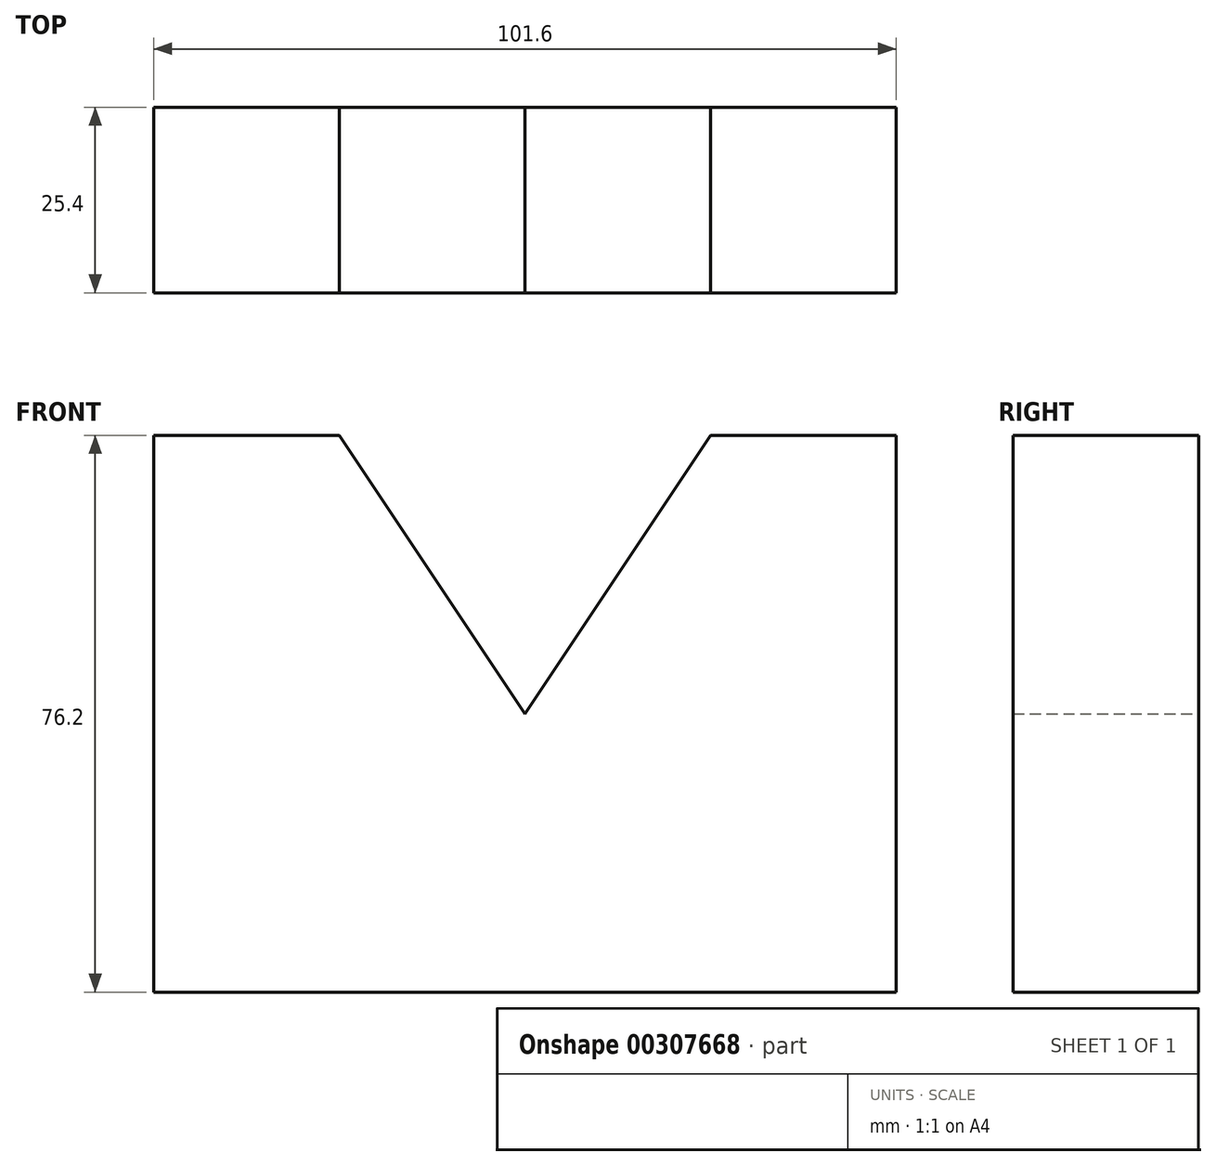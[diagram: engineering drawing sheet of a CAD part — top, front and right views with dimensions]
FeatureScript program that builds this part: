
annotation { "Feature Type Name" : "Feature", "Feature Type Description" : "" }
export const myFeature = defineFeature(function(context is Context, id is Id, definition is map)
    precondition{}
    {
        {
            var Q0;
            Q0=qCreatedBy(makeId("Front.planeOp"),FACE);
            var sketch = newSketch(context, id + "F0", { "sketchPlane" : qUnion([Q0])});
            skLineSegment(sketch, "E0", {"start": v(58.87, -69.34) * mm, "end": v(58.87, 6.86) * mm});
            skLineSegment(sketch, "E1", {"start": v(58.87, 6.86) * mm, "end": v(33.47, 6.86) * mm});
            skLineSegment(sketch, "E2", {"start": v(33.47, 6.86) * mm, "end": v(8.07, -31.24) * mm});
            skLineSegment(sketch, "E3", {"start": v(58.87, -69.34) * mm, "end": v(-42.73, -69.34) * mm});
            skLineSegment(sketch, "E4", {"start": v(-42.73, -69.34) * mm, "end": v(-42.73, 6.86) * mm});
            skLineSegment(sketch, "E5", {"start": v(-42.73, 6.86) * mm, "end": v(-17.33, 6.86) * mm});
            skLineSegment(sketch, "E6", {"start": v(-17.33, 6.86) * mm, "end": v(8.07, -31.24) * mm});
            skSolve(sketch);
        }
        {
            var Q0;
            Q0=makeQuery(id+"F0.imprint","IMPRINT",FACE,{"disambiguationData":[TD([[makeQuery(id+"F0.imprint","IMPRINT",EDGE,{"derivedFrom":sQuery(id+"F0.wireOp",EDGE,"E0")}),1.0]])]});
            extrude(context, id + "F1", {"entities" : qUnion([Q0]), "depth" : 25.4 * mm});
        }
    });
